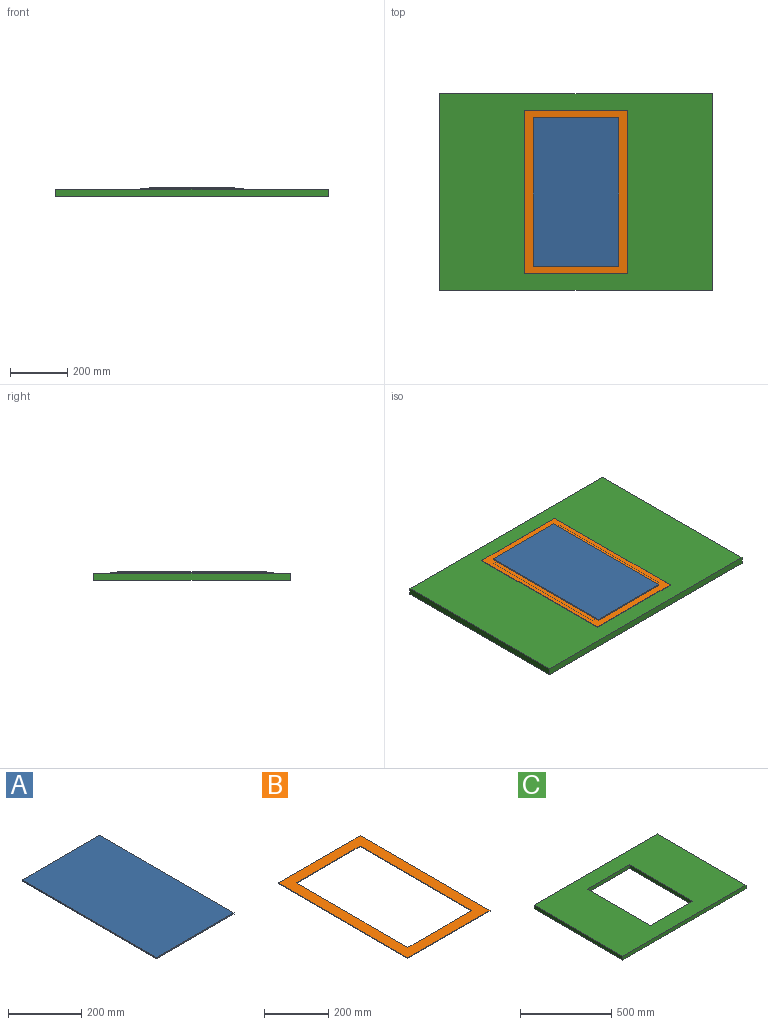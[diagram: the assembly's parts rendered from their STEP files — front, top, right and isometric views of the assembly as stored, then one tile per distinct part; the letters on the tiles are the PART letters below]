
ASSEMBLY  parts=3 mates=2
PART A: 6 faces, bbox 300x520x4 mm
  f0: plane 300x4mm, normal (0,1,0), area 1200mm2, adj f1,f3,f4,f5
  f1: plane 520x4mm, normal (-1,0,0), area 2080mm2, adj f0,f2,f4,f5
  f2: plane 300x4mm, normal (0,-1,0), area 1200mm2, adj f1,f3,f4,f5
  f3: plane 520x4mm, normal (1,0,0), area 2080mm2, adj f0,f2,f4,f5
  f4: plane 520x300mm, normal (0,0,1), area 156000mm2, adj f0,f1,f2,f3
  f5: plane 520x300mm, normal (0,0,-1), area 156000mm2, adj f0,f1,f2,f3
PART B: 10 faces, bbox 360x570x2 mm
  f0: plane 360x2mm, normal (0,1,0), area 720mm2, adj f1,f7,f8,f9
  f1: plane 570x2mm, normal (-1,0,0), area 1140mm2, adj f0,f2,f8,f9
  f2: plane 360x2mm, normal (0,-1,0), area 720mm2, adj f1,f7,f8,f9
  f3: plane 490x2mm, normal (1,0,0), area 980mm2, adj f4,f6,f8,f9
  f4: plane 280x2mm, normal (0,-1,0), area 560mm2, adj f3,f5,f8,f9
  f5: plane 490x2mm, normal (-1,0,0), area 980mm2, adj f4,f6,f8,f9
  f6: plane 280x2mm, normal (0,1,0), area 560mm2, adj f3,f5,f8,f9
  f7: plane 570x2mm, normal (1,0,0), area 1140mm2, adj f0,f2,f8,f9
  f8: plane 570x360mm, normal (0,0,1), area 68000mm2, adj f0,f1,f2,f3,f4,f5,f6,f7
  f9: plane 570x360mm, normal (0,0,-1), area 68000mm2, adj f0,f1,f2,f3,f4,f5,f6,f7
PART C: 10 faces, bbox 952.7x687.6x25 mm
  f0: plane 952.7x25mm, normal (0,1,0), area 23817.5mm2, adj f1,f7,f8,f9
  f1: plane 687.6x25mm, normal (-1,0,0), area 17190mm2, adj f0,f2,f8,f9
  f2: plane 952.7x25mm, normal (0,-1,0), area 23817.5mm2, adj f1,f7,f8,f9
  f3: plane 490x25mm, normal (1,0,0), area 12250mm2, adj f4,f6,f8,f9
  f4: plane 328x25mm, normal (0,-1,0), area 8200mm2, adj f3,f5,f8,f9
  f5: plane 490x25mm, normal (-1,0,0), area 12250mm2, adj f4,f6,f8,f9
  f6: plane 328x25mm, normal (0,1,0), area 8200mm2, adj f3,f5,f8,f9
  f7: plane 687.6x25mm, normal (1,0,0), area 17190mm2, adj f0,f2,f8,f9
  f8: plane 952.7x687.6mm, normal (0,0,-1), area 494357.6mm2, adj f0,f1,f2,f3,f4,f5,f6,f7
  f9: plane 952.7x687.6mm, normal (0,0,1), area 494357.6mm2, adj f0,f1,f2,f3,f4,f5,f6,f7
PLACE A rot(axis=(1,0,0),180deg) t=(0,0,6)mm
PLACE B at identity
PLACE C at identity fixed
MATE fastened B.f9 <-> C.f9  axis (0,0,1) through (0,0,0)mm
MATE fastened A.f4 <-> B.f8  axis (0,0,-1) through (0,0,2)mm
